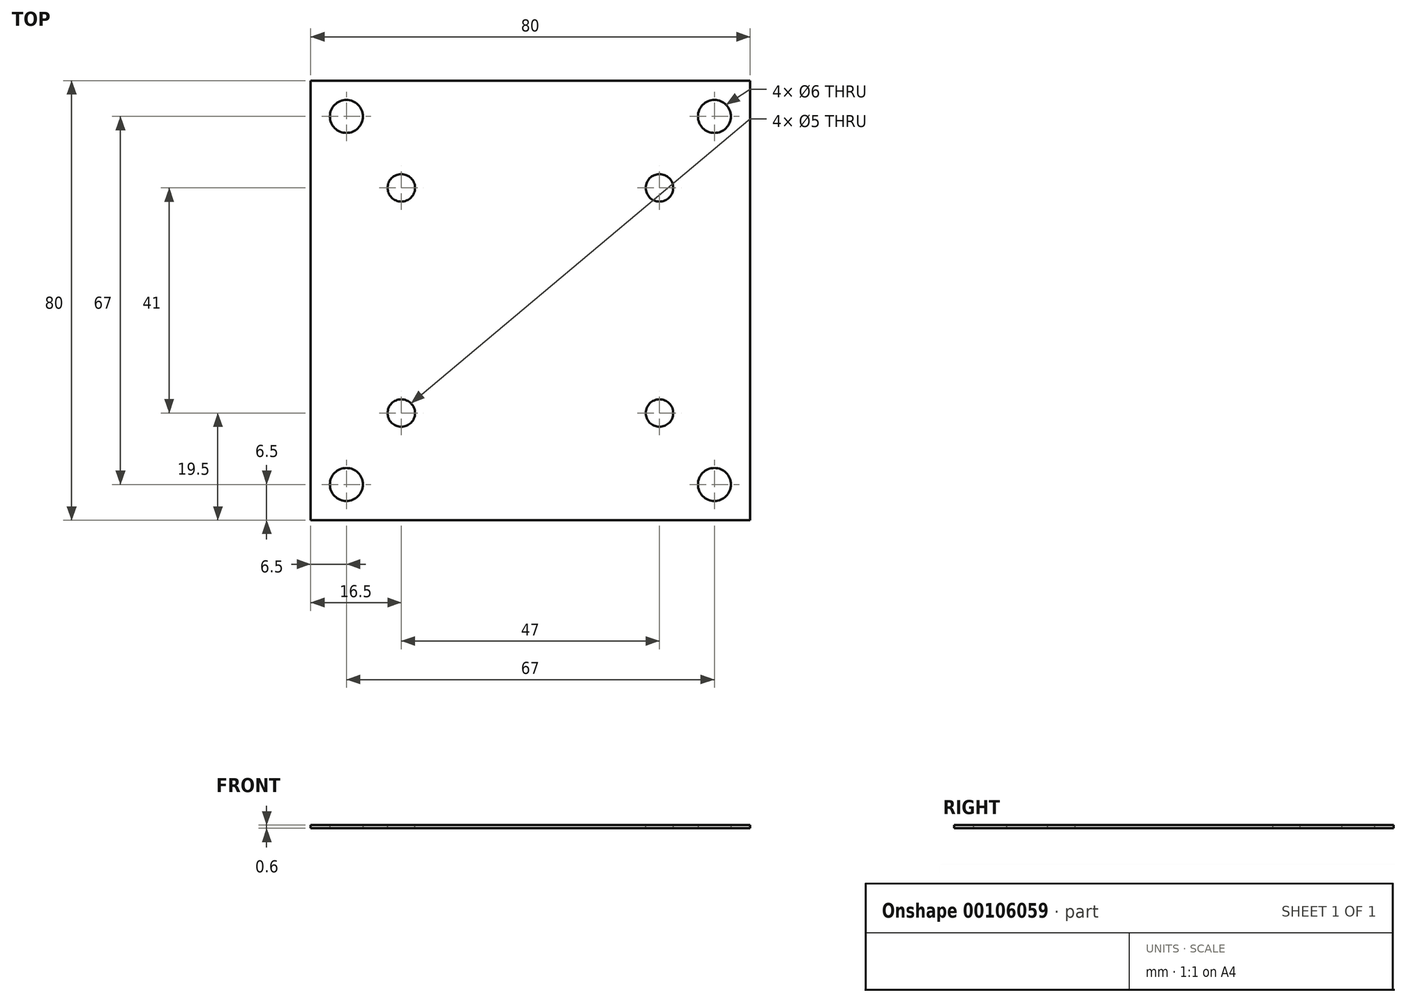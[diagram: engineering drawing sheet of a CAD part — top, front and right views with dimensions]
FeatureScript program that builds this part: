
annotation { "Feature Type Name" : "Feature", "Feature Type Description" : "" }
export const myFeature = defineFeature(function(context is Context, id is Id, definition is map)
    precondition{}
    {
        {
            var Q0;
            Q0=qCreatedBy(makeId("Top.planeOp"),FACE);
            var sketch = newSketch(context, id + "F0", { "sketchPlane" : qUnion([Q0])});
            skLineSegment(sketch, "E0.bottom", {"start": v(0, 0) * mm, "end": v(80, 0) * mm});
            skLineSegment(sketch, "E0.top", {"start": v(0, 80) * mm, "end": v(80, 80) * mm});
            skLineSegment(sketch, "E0.left", {"start": v(0, 0) * mm, "end": v(0, 80) * mm});
            skLineSegment(sketch, "E0.right", {"start": v(80, 0) * mm, "end": v(80, 80) * mm});
            skCircle(sketch, "E1", {"center": v(6.5, 73.5) * mm, "radius": 3 * mm});
            skCircle(sketch, "E2.0.1.0", {"center": v(6.5, 6.5) * mm, "radius": 3 * mm});
            skCircle(sketch, "E2.1.0.0", {"center": v(73.5, 73.5) * mm, "radius": 3 * mm});
            skCircle(sketch, "E2.1.1.0", {"center": v(73.5, 6.5) * mm, "radius": 3 * mm});
            skLineSegment(sketch, "E2.direction1", {"start": v(6.5, 73.5) * mm, "end": v(73.5, 73.5) * mm, "construction": true});
            skLineSegment(sketch, "E2.direction2", {"start": v(6.5, 73.5) * mm, "end": v(6.5, 6.5) * mm, "construction": true});
            skLineSegment(sketch, "E3.bottom", {"start": v(0, 80) * mm, "end": v(10, 80) * mm});
            skLineSegment(sketch, "E3.top", {"start": v(0, 110) * mm, "end": v(10, 110) * mm});
            skLineSegment(sketch, "E3.left", {"start": v(0, 80) * mm, "end": v(0, 110) * mm});
            skLineSegment(sketch, "E3.right", {"start": v(10, 80) * mm, "end": v(10, 110) * mm});
            skLineSegment(sketch, "E4.bottom", {"start": v(80, 80) * mm, "end": v(70, 80) * mm});
            skLineSegment(sketch, "E4.top", {"start": v(80, 110) * mm, "end": v(70, 110) * mm});
            skLineSegment(sketch, "E4.left", {"start": v(80, 80) * mm, "end": v(80, 110) * mm});
            skLineSegment(sketch, "E4.right", {"start": v(70, 80) * mm, "end": v(70, 110) * mm});
            skSolve(sketch);
        }
        {
            var Q0;
            Q0=makeQuery(id+"F0.imprint","IMPRINT",FACE,{"disambiguationData":[TD([[makeQuery(id+"F0.imprint","IMPRINT",EDGE,{"derivedFrom":sQuery(id+"F0.wireOp",EDGE,"E0.bottom")}),1.0]])]});
            var Q1;
            Q1=makeQuery(id+"F0.imprint","IMPRINT",FACE,{"disambiguationData":[TD([[makeQuery(id+"F0.imprint","IMPRINT",EDGE,{"derivedFrom":sQuery(id+"F0.wireOp",EDGE,"E3.bottom")}),1.0]])]});
            var Q2;
            Q2=makeQuery(id+"F0.imprint","IMPRINT",FACE,{"disambiguationData":[TD([[makeQuery(id+"F0.imprint","IMPRINT",EDGE,{"derivedFrom":sQuery(id+"F0.wireOp",EDGE,"E4.bottom")}),-1.0]])]});
            extrude(context, id + "F1", {"entities" : qUnion([Q0, Q1, Q2]), "depth" : 0.6 * mm});
        }
        {
            var Q0;
            Q0=makeQuery(id+"F1.opExtrude","CAP_FACE",FACE,{"disambiguationData":[OSD([sQuery(id+"F0.wireOp",EDGE,"E0.bottom"),sQuery(id+"F0.wireOp",EDGE,"E0.top"),sQuery(id+"F0.wireOp",EDGE,"E0.left"),sQuery(id+"F0.wireOp",EDGE,"E0.right"),sQuery(id+"F0.wireOp",EDGE,"E1"),sQuery(id+"F0.wireOp",EDGE,"E2.0.1.0"),sQuery(id+"F0.wireOp",EDGE,"E2.1.0.0"),sQuery(id+"F0.wireOp",EDGE,"E2.1.1.0"),sQuery(id+"F0.wireOp",EDGE,"E3.top"),sQuery(id+"F0.wireOp",EDGE,"E3.left"),sQuery(id+"F0.wireOp",EDGE,"E3.right"),sQuery(id+"F0.wireOp",EDGE,"E4.top"),sQuery(id+"F0.wireOp",EDGE,"E4.left"),sQuery(id+"F0.wireOp",EDGE,"E4.right")])],"isStart":false});
            var sketch = newSketch(context, id + "F2", { "sketchPlane" : qUnion([Q0])});
            skCircle(sketch, "E5", {"center": v(16.5, 60.5) * mm, "radius": 2.5 * mm});
            skCircle(sketch, "E6", {"center": v(63.5, 60.5) * mm, "radius": 2.5 * mm});
            skCircle(sketch, "E7", {"center": v(63.5, 19.5) * mm, "radius": 2.5 * mm});
            skCircle(sketch, "E8", {"center": v(16.5, 19.5) * mm, "radius": 2.5 * mm});
            skSolve(sketch);
        }
        {
            var Q0;
            Q0 = qSketchRegion(id + "F2", true);
            extrude(context, id + "F3", {"entities" : qUnion([Q0]), "operationType" : NewBodyOperationType.REMOVE, "endBound" : BoundingType.THROUGH_ALL, "oppositeDirection" : true, "depth" : 25 * mm});
        }
    });
